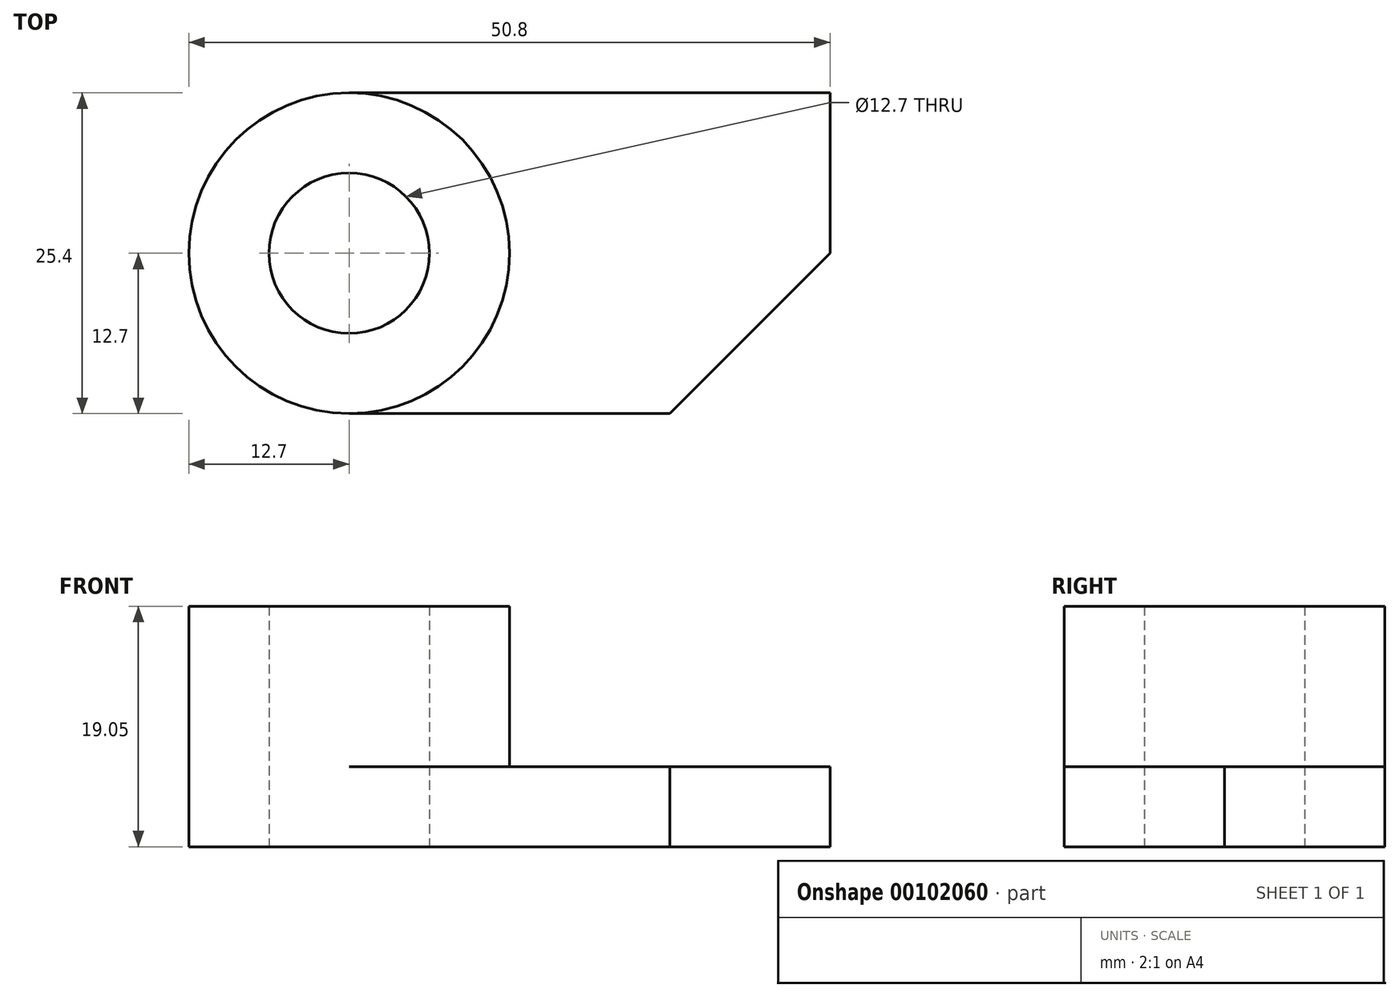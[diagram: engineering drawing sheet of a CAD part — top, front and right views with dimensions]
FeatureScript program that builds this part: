
annotation { "Feature Type Name" : "Feature", "Feature Type Description" : "" }
export const myFeature = defineFeature(function(context is Context, id is Id, definition is map)
    precondition{}
    {
        {
            var Q0;
            Q0=qCreatedBy(makeId("Top.planeOp"),FACE);
            var sketch = newSketch(context, id + "F0", { "sketchPlane" : qUnion([Q0])});
            skLineSegment(sketch, "E0", {"start": v(0, 0) * mm, "end": v(0, 25.4) * mm});
            skLineSegment(sketch, "E1", {"start": v(0, 25.4) * mm, "end": v(38.1, 25.4) * mm});
            skLineSegment(sketch, "E2", {"start": v(38.1, 25.4) * mm, "end": v(38.1, 12.7) * mm});
            skLineSegment(sketch, "E3", {"start": v(38.1, 12.7) * mm, "end": v(25.4, 0) * mm});
            skLineSegment(sketch, "E4", {"start": v(25.4, 0) * mm, "end": v(0, 0) * mm});
            skSolve(sketch);
        }
        {
            var Q0;
            Q0 = qSketchRegion(id + "F0", true);
            extrude(context, id + "F1", {"entities" : qUnion([Q0]), "depth" : 6.35 * mm});
        }
        {
            var Q0;
            Q0=qCreatedBy(makeId("Top.planeOp"),FACE);
            var sketch = newSketch(context, id + "F2", { "sketchPlane" : qUnion([Q0])});
            skCircle(sketch, "E5", {"center": v(0, 12.7) * mm, "radius": 12.7 * mm});
            skPoint(sketch, "E5.first.point", {"position": v(0, 25.4) * mm});
            skPoint(sketch, "E5.second.point", {"position": v(0, 0) * mm});
            skPoint(sketch, "E5.third.point", {"position": v(-12.64, 11.52) * mm});
            skCircle(sketch, "E6", {"center": v(0, 12.7) * mm, "radius": 6.35 * mm});
            skSolve(sketch);
        }
        {
            var Q0;
            Q0=makeQuery(id+"F2.imprint","IMPRINT",FACE,{"disambiguationData":[TD([[makeQuery(id+"F2.imprint","IMPRINT",EDGE,{"derivedFrom":sQuery(id+"F2.wireOp",EDGE,"E5")}),1.0]])]});
            extrude(context, id + "F3", {"entities" : qUnion([Q0]), "operationType" : NewBodyOperationType.ADD, "depth" : 19.05 * mm});
        }
        {
            var Q0;
            Q0=makeQuery(id+"F2.imprint","IMPRINT",FACE,{"disambiguationData":[TD([[makeQuery(id+"F2.imprint","IMPRINT",EDGE,{"derivedFrom":sQuery(id+"F2.wireOp",EDGE,"E6")}),1.0]])]});
            extrude(context, id + "F4", {"entities" : qUnion([Q0]), "operationType" : NewBodyOperationType.REMOVE, "depth" : 25.4 * mm});
        }
    });
